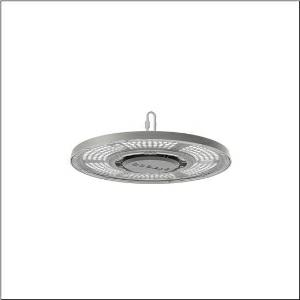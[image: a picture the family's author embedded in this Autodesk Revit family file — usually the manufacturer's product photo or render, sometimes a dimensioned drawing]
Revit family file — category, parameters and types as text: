
# Revit family: highbay_31-s_51hc427a4jmb
name_source: partatom
category: Lighting Fixtures
units: mm (PartAtom-declared; Revit-internal decimal feet)

## family parameters
Cut with Voids When Loaded = No
Host = Face
Light Source = No
Part Type = Normal
Room Calculation Point = No
Round Connector Dimension = Use Diameter
Shared = No

## types (1)
- Highbay 31-S (1 x LED, 20000 lm, 134 W, 4000K)
    Apparent Load = 134 VA
    CIE Flux Codes = 77 99 100 100 100
    Color Rendering = 80
    Color Temperature = 4000K
    Default Elevation = 1800 mm
    Description = Highbay 31-S, high bay luminaire, primary light control with lens, of PC, primary optical cover: cover panel, of PC, transparent, light emission: direct distribution, primary light characteristic: rotationally symmetric, installation type: suspended mounting, surface-mounted, LED, rated luminous flux: 20.000lm, luminous efficacy: 150lm/W, light colour: 840, colour temperature: 4000K, control gear: ON/OFF, with cable, 3x 1.0mm², free wire ends, mains connection: 220..240V, AC/DC, 0/50..60Hz, cable length: 1,5m, rated input power: 134W, housing, rotationally symmetric, of diecast aluminium, powder-coated, grey aluminium (RAL 9007), with hook on luminaire side, incl. screw, diameter: 339mm, protection rating (complete): IP65, insulation class (complete): insulation class I (protective earthing), certification: CE, ENEC, UKCA, protection symbol: D, impact resistance: IK08, permissible operating ambient temperature: -30..+45°C, standard: EN 60598-2-22, EN 60598, corresponds to IFS (International Featured Standards) requirements for safety and quality in the food industry, packaging unit: 1 piece
    Height = 141 mm
    Lamp = 1 x LED
    Lamp Light Flux = 20000 lm
    Lamp Power = 134 W
    Lamp count = 1
    Length = 339 mm
    Luminous efficacy = 149 lm/W
    Manufacturer = Siteco
    ModVariant = No
    Model = 51HC427A4JMB
    Mounting Place = Ceiling
    Mounting Type = Pendant
    Number of Poles = 1
    OnlyDefault = Yes
    Power Factor = 1
    Product Name = Highbay 31-S
    Product group = high bay luminaire
    ProductGroupID = 901
    Protection Class = Protection class I
    Protection Degree = IP 65
    RLX_Detail_Level = 1
    RLX_Emergency_Light_Flux = 0 lm
    RLX_Emergency_Type = 0
    RLX_Emergency_Type_DB = No
    RlxData = <blob elided: 163009 chars, md5=48b8dc79>
    Socket = socket
    Standby Power = 0 W
    System Light Flux = 20000 lm
    System Power = 134 W
    Type Comments = Product without accessories
    Type Image = l_1007237.jpg
    URL = http://relux.com
    VarID = ---
    Voltage = 0 V
    Weight = 0.00 kg
    Width = 0 mm  [stored 0 ft]

note: [stored X ft] marks values corroborated as IEEE doubles in the binary element streams (Revit-internal decimal feet)

## geometry (parser evidence)
native form markers: Blend x4, Sweep x10
no freeform markers — native parametric forms only
